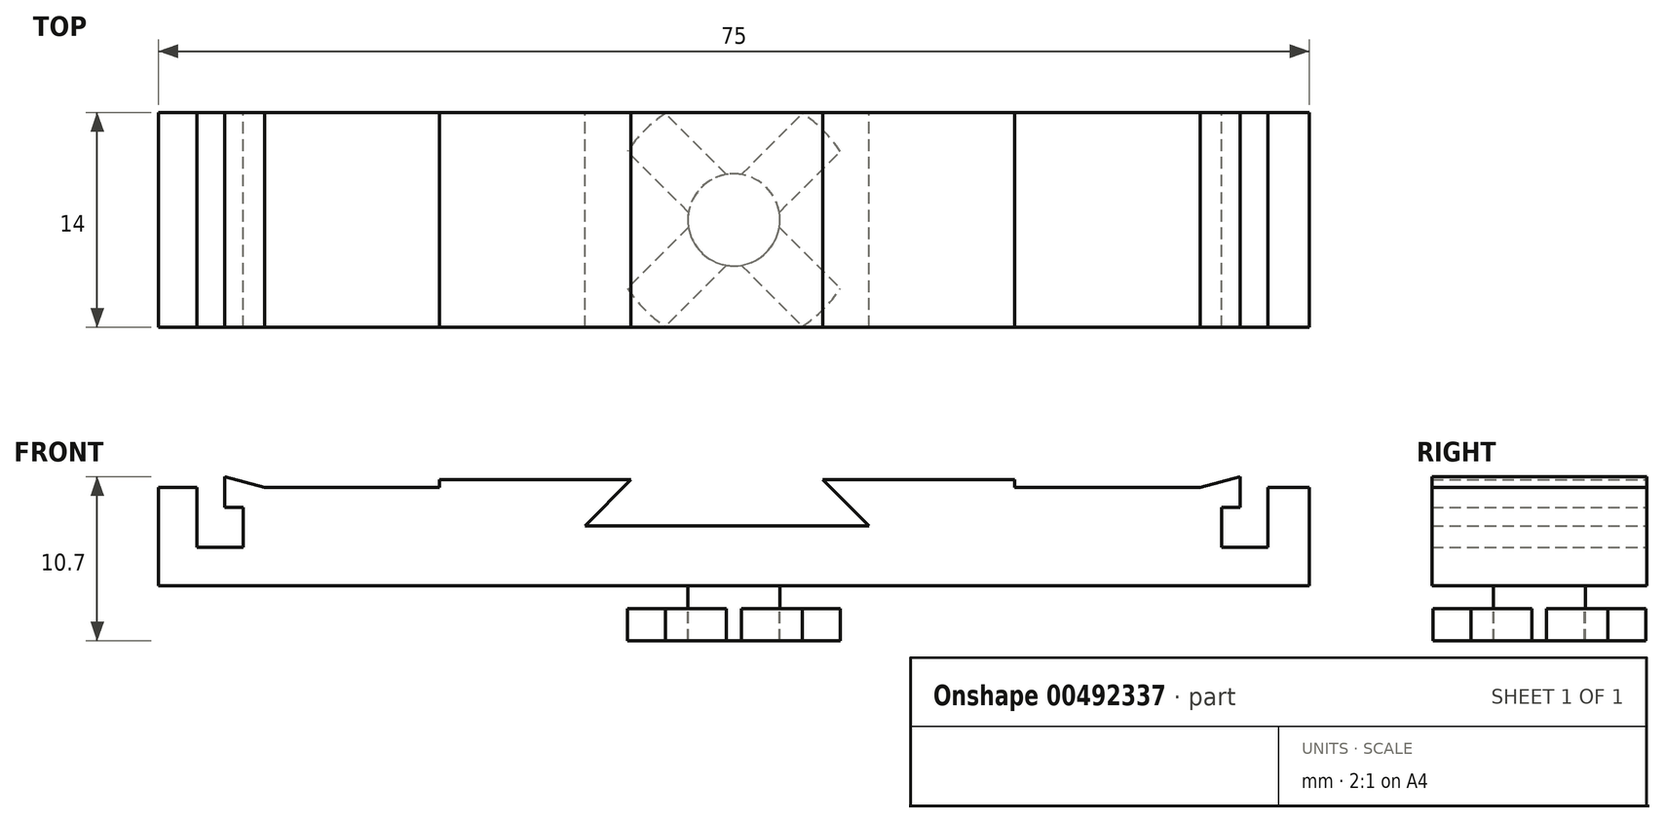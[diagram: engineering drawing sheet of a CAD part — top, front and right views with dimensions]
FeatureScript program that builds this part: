
annotation { "Feature Type Name" : "Feature", "Feature Type Description" : "" }
export const myFeature = defineFeature(function(context is Context, id is Id, definition is map)
    precondition{}
    {
        {
            var Q0;
            Q0=qCreatedBy(makeId("Front.planeOp"),FACE);
            var sketch = newSketch(context, id + "F0", { "sketchPlane" : qUnion([Q0])});
            skLineSegment(sketch, "E0", {"start": v(0, 0) * mm, "end": v(-75, 0) * mm});
            skLineSegment(sketch, "E1", {"start": v(-75, 0) * mm, "end": v(-75, 6.4) * mm});
            skLineSegment(sketch, "E2", {"start": v(-75, 6.4) * mm, "end": v(-72.5, 6.4) * mm});
            skLineSegment(sketch, "E3", {"start": v(-72.5, 6.4) * mm, "end": v(-72.5, 2.5) * mm});
            skLineSegment(sketch, "E4", {"start": v(-72.5, 2.5) * mm, "end": v(-69.5, 2.5) * mm});
            skLineSegment(sketch, "E5", {"start": v(-69.5, 2.5) * mm, "end": v(-69.5, 5.1) * mm});
            skLineSegment(sketch, "E6", {"start": v(-69.5, 5.1) * mm, "end": v(-70.7, 5.1) * mm});
            skLineSegment(sketch, "E7", {"start": v(-70.7, 5.1) * mm, "end": v(-70.7, 6.4) * mm});
            skLineSegment(sketch, "E8", {"start": v(-68.1, 6.4) * mm, "end": v(-56.7, 6.4) * mm});
            skLineSegment(sketch, "E9", {"start": v(-44.7, 6.4) * mm, "end": v(-47.2, 3.9) * mm});
            skLineSegment(sketch, "E10", {"start": v(-47.2, 3.9) * mm, "end": v(-28.7, 3.9) * mm});
            skLineSegment(sketch, "E11", {"start": v(-28.7, 3.9) * mm, "end": v(-31.2, 6.4) * mm});
            skLineSegment(sketch, "E12", {"start": v(-19.2, 6.4) * mm, "end": v(-7.1, 6.4) * mm});
            skLineSegment(sketch, "E13", {"start": v(-4.5, 6.4) * mm, "end": v(-4.5, 5.1) * mm});
            skLineSegment(sketch, "E14", {"start": v(-4.5, 5.1) * mm, "end": v(-5.7, 5.1) * mm});
            skLineSegment(sketch, "E15", {"start": v(-5.7, 5.1) * mm, "end": v(-5.7, 2.5) * mm});
            skLineSegment(sketch, "E16", {"start": v(-5.7, 2.5) * mm, "end": v(-2.7, 2.5) * mm});
            skLineSegment(sketch, "E17", {"start": v(-2.7, 2.5) * mm, "end": v(-2.7, 6.4) * mm});
            skLineSegment(sketch, "E18", {"start": v(-2.7, 6.4) * mm, "end": v(0, 6.4) * mm});
            skLineSegment(sketch, "E19", {"start": v(0, 6.4) * mm, "end": v(0, 0) * mm});
            skLineSegment(sketch, "E20", {"start": v(-44.7, 6.4) * mm, "end": v(-44.2, 6.9) * mm});
            skLineSegment(sketch, "E21", {"start": v(-44.2, 6.9) * mm, "end": v(-56.7, 6.9) * mm});
            skLineSegment(sketch, "E22", {"start": v(-56.7, 6.9) * mm, "end": v(-56.7, 6.4) * mm});
            skLineSegment(sketch, "E23", {"start": v(-31.2, 6.4) * mm, "end": v(-31.7, 6.9) * mm});
            skLineSegment(sketch, "E24", {"start": v(-31.7, 6.9) * mm, "end": v(-19.2, 6.9) * mm});
            skLineSegment(sketch, "E25", {"start": v(-19.2, 6.9) * mm, "end": v(-19.2, 6.4) * mm});
            skLineSegment(sketch, "E26", {"start": v(-70.7, 6.4) * mm, "end": v(-70.7, 7.1) * mm});
            skLineSegment(sketch, "E27", {"start": v(-70.7, 7.1) * mm, "end": v(-68.1, 6.4) * mm});
            skLineSegment(sketch, "E28", {"start": v(-4.5, 6.4) * mm, "end": v(-4.5, 7.1) * mm});
            skLineSegment(sketch, "E29", {"start": v(-4.5, 7.1) * mm, "end": v(-7.1, 6.4) * mm});
            skSolve(sketch);
        }
        {
            var Q0;
            Q0=makeQuery(id+"F0.imprint","IMPRINT",FACE,{"disambiguationData":[TD([[makeQuery(id+"F0.imprint","IMPRINT",EDGE,{"derivedFrom":sQuery(id+"F0.wireOp",EDGE,"E0")}),-1.0]])]});
            extrude(context, id + "F1", {"entities" : qUnion([Q0]), "endBound" : BoundingType.SYMMETRIC, "depth" : 14 * mm});
        }
        {
            var Q0;
            Q0=makeQuery(id+"F1.opExtrude","SWEPT_FACE",FACE,{"disambiguationData":[OSD([sQuery(id+"F0.wireOp",EDGE,"E0")])]});
            var sketch = newSketch(context, id + "F2", { "sketchPlane" : qUnion([Q0])});
            skLineSegment(sketch, "E30", {"start": v(-37.5, -7) * mm, "end": v(-37.5, 7) * mm, "construction": true});
            skCircle(sketch, "E31", {"center": v(-37.5, 0) * mm, "radius": 3 * mm});
            skArc(sketch, "E32", {"start": v(-41.96, 6.94) * mm, "mid": v(-43.33, 5.83) * mm, "end": v(-44.44, 4.46) * mm});
            skLineSegment(sketch, "E33", {"start": v(-37.5, 0) * mm, "end": v(-32.41, 5.09) * mm, "construction": true});
            skLineSegment(sketch, "E34", {"start": v(-37.01, 2.96) * mm, "end": v(-33.04, 6.94) * mm});
            skLineSegment(sketch, "E35", {"start": v(-34.54, 0.49) * mm, "end": v(-30.56, 4.46) * mm});
            skLineSegment(sketch, "E36.1.0", {"start": v(-40.46, 0.49) * mm, "end": v(-44.44, 4.46) * mm});
            skLineSegment(sketch, "E36.1.1", {"start": v(-37.99, 2.96) * mm, "end": v(-41.96, 6.94) * mm});
            skLineSegment(sketch, "E36.2.0", {"start": v(-37.99, -2.96) * mm, "end": v(-41.96, -6.94) * mm});
            skLineSegment(sketch, "E36.2.1", {"start": v(-40.46, -0.49) * mm, "end": v(-44.44, -4.46) * mm});
            skLineSegment(sketch, "E36.3.0", {"start": v(-34.54, -0.49) * mm, "end": v(-30.56, -4.46) * mm});
            skLineSegment(sketch, "E36.3.1", {"start": v(-37.01, -2.96) * mm, "end": v(-33.04, -6.94) * mm});
            skArc(sketch, "E37.trimOffspring", {"start": v(-44.44, -4.46) * mm, "mid": v(-43.33, -5.83) * mm, "end": v(-41.96, -6.94) * mm});
            skArc(sketch, "E38.trimOffspring", {"start": v(-30.56, 4.46) * mm, "mid": v(-31.67, 5.83) * mm, "end": v(-33.04, 6.94) * mm});
            skArc(sketch, "E39.trimOffspring", {"start": v(-33.04, -6.94) * mm, "mid": v(-31.67, -5.83) * mm, "end": v(-30.56, -4.46) * mm});
            skSolve(sketch);
        }
        {
            var Q0;
            {var subQ0=sQuery(id+"F2.wireOp",EDGE,"E31");var subQ4=makeQuery(id+"F2.imprint","INTERSECT",VERTEX,{"derivedFrom":[subQ0,sQuery(id+"F2.wireOp",EDGE,"E34")]});Q0=makeQuery(id+"F2.imprint","IMPRINT",FACE,{"disambiguationData":[TD([[makeQuery(id+"F2.imprint","IMPRINT",EDGE,{"disambiguationData":[TD([[subQ4,1.0]])],"derivedFrom":subQ0}),1.0]])]});}
            extrude(context, id + "F3", {"entities" : qUnion([Q0]), "operationType" : NewBodyOperationType.ADD, "depth" : 3.6 * mm});
        }
        {
            var Q0;
            Q0=makeQuery(id+"F2.imprint","IMPRINT",FACE,{"disambiguationData":[TD([[makeQuery(id+"F2.imprint","IMPRINT",EDGE,{"derivedFrom":sQuery(id+"F2.wireOp",EDGE,"E32")}),1.0]])]});
            var Q1;
            {var subQ0=sQuery(id+"F2.wireOp",EDGE,"E34");Q1=makeQuery(id+"F2.imprint","IMPRINT",FACE,{"disambiguationData":[TD([[makeQuery(id+"F2.imprint","IMPRINT",EDGE,{"derivedFrom":subQ0}),-1.0]])]});}
            var Q2;
            {var subQ0=sQuery(id+"F2.wireOp",EDGE,"E36.2.0");Q2=makeQuery(id+"F2.imprint","IMPRINT",FACE,{"disambiguationData":[TD([[makeQuery(id+"F2.imprint","IMPRINT",EDGE,{"derivedFrom":subQ0}),-1.0]])]});}
            var Q3;
            {var subQ0=sQuery(id+"F2.wireOp",EDGE,"E36.3.0");Q3=makeQuery(id+"F2.imprint","IMPRINT",FACE,{"disambiguationData":[TD([[makeQuery(id+"F2.imprint","IMPRINT",EDGE,{"derivedFrom":subQ0}),-1.0]])]});}
            extrude(context, id + "F4", {"entities" : qUnion([Q0, Q1, Q2, Q3]), "operationType" : NewBodyOperationType.ADD, "depth" : 3.6 * mm, "hasSecondDirection" : true, "secondDirectionOppositeDirection" : false, "secondDirectionDepth" : 1.5 * mm});
        }
    });
